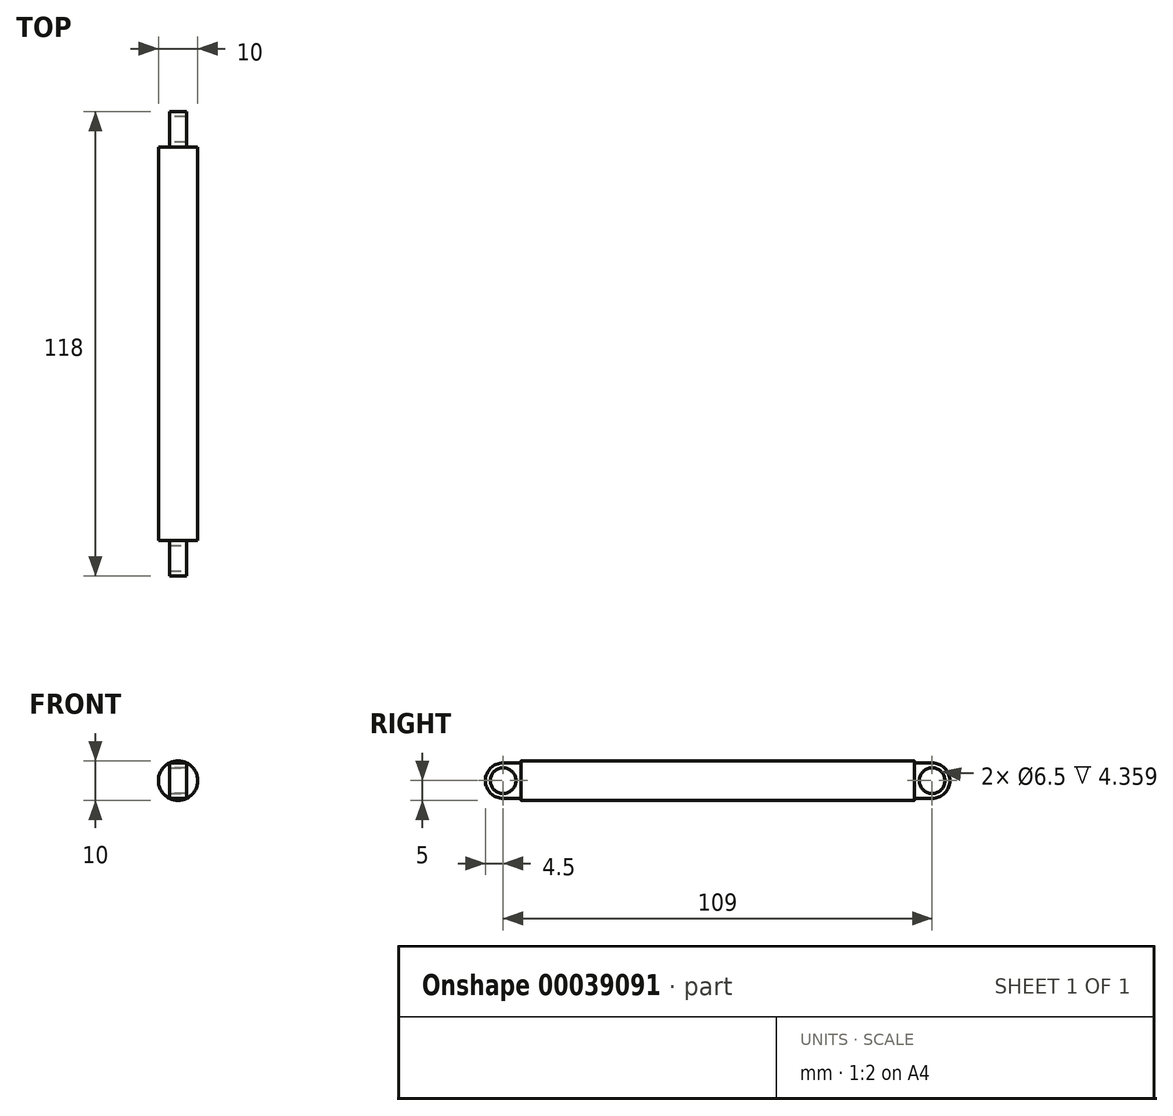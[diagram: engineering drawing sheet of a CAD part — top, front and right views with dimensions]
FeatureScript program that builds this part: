
annotation { "Feature Type Name" : "Feature", "Feature Type Description" : "" }
export const myFeature = defineFeature(function(context is Context, id is Id, definition is map)
    precondition{}
    {
        {
            var Q0;
            Q0=qCreatedBy(makeId("Top.planeOp"),FACE);
            var sketch = newSketch(context, id + "F0", { "sketchPlane" : qUnion([Q0])});
            skLineSegment(sketch, "E0.bottom", {"start": v(0, 100) * mm, "end": v(-5, 100) * mm});
            skLineSegment(sketch, "E0.top", {"start": v(0, 0) * mm, "end": v(-5, 0) * mm});
            skLineSegment(sketch, "E0.left", {"start": v(0, 100) * mm, "end": v(0, 0) * mm});
            skLineSegment(sketch, "E0.right", {"start": v(-5, 100) * mm, "end": v(-5, 0) * mm});
            skSolve(sketch);
        }
        {
            var Q0;
            Q0 = qSketchRegion(id + "F0", true);
            var Q1;
            Q1=sQuery(id+"F0.wireOp",EDGE,"E0.left");
            revolve(context, id + "F1", {"entities" : qUnion([Q0]), "axis" : qUnion([Q1]), "revolveType" : RevolveType.FULL});
        }
        {
            var Q0;
            Q0=makeQuery(id+"F1.opRevolve","SWEPT_FACE",FACE,{"disambiguationData":[OSD([sQuery(id+"F0.wireOp",EDGE,"E0.top")])]});
            var sketch = newSketch(context, id + "F2", { "sketchPlane" : qUnion([Q0])});
            skLineSegment(sketch, "E1.bottom", {"start": v(-2.18, 4.5) * mm, "end": v(2.18, 4.5) * mm});
            skLineSegment(sketch, "E1.top", {"start": v(-2.18, -4.5) * mm, "end": v(2.18, -4.5) * mm});
            skLineSegment(sketch, "E1.left", {"start": v(-2.18, 4.5) * mm, "end": v(-2.18, -4.5) * mm});
            skLineSegment(sketch, "E1.right", {"start": v(2.18, 4.5) * mm, "end": v(2.18, -4.5) * mm});
            skSolve(sketch);
        }
        {
            var Q0;
            Q0 = qSketchRegion(id + "F2", true);
            extrude(context, id + "F3", {"entities" : qUnion([Q0]), "operationType" : NewBodyOperationType.ADD, "depth" : 9 * mm});
        }
        {
            var Q0;
            Q0=makeQuery(id+"F3.opExtrude","SWEPT_FACE",FACE,{"disambiguationData":[OSD([sQuery(id+"F2.wireOp",EDGE,"E1.right")])]});
            var sketch = newSketch(context, id + "F4", { "sketchPlane" : qUnion([Q0])});
            skCircle(sketch, "E2", {"center": v(-4.5, 0) * mm, "radius": 3.25 * mm});
            skSolve(sketch);
        }
        {
            var Q0;
            Q0 = qSketchRegion(id + "F4", true);
            extrude(context, id + "F5", {"entities" : qUnion([Q0]), "operationType" : NewBodyOperationType.REMOVE, "oppositeDirection" : true, "depth" : 5 * mm});
        }
        {
            var Q0;
            Q0=makeQuery(id+"F3.opExtrude","CAP_EDGE",EDGE,{"disambiguationData":[OSD([sQuery(id+"F2.wireOp",EDGE,"E1.bottom")])],"isStart":false});
            var Q1;
            Q1=makeQuery(id+"F3.opExtrude","CAP_EDGE",EDGE,{"disambiguationData":[OSD([sQuery(id+"F2.wireOp",EDGE,"E1.top")])],"isStart":false});
            fillet(context, id + "F6", {"entities" : qUnion([Q0, Q1]), "radius" : 4.5 * mm, "tangentPropagation" : true, "allowEdgeOverflow" : false});
        }
        {
            var Q0;
            Q0=makeQuery(id+"F1.opRevolve","SWEPT_FACE",FACE,{"disambiguationData":[OSD([sQuery(id+"F0.wireOp",EDGE,"E0.bottom")])]});
            var sketch = newSketch(context, id + "F7", { "sketchPlane" : qUnion([Q0])});
            skLineSegment(sketch, "E3.bottom", {"start": v(-2.18, 4.5) * mm, "end": v(2.18, 4.5) * mm});
            skLineSegment(sketch, "E3.top", {"start": v(-2.18, -4.5) * mm, "end": v(2.18, -4.5) * mm});
            skLineSegment(sketch, "E3.left", {"start": v(-2.18, 4.5) * mm, "end": v(-2.18, -4.5) * mm});
            skLineSegment(sketch, "E3.right", {"start": v(2.18, 4.5) * mm, "end": v(2.18, -4.5) * mm});
            skSolve(sketch);
        }
        {
            var Q0;
            Q0 = qSketchRegion(id + "F7", true);
            extrude(context, id + "F8", {"entities" : qUnion([Q0]), "operationType" : NewBodyOperationType.ADD, "depth" : 9 * mm});
        }
        {
            var Q0;
            Q0=makeQuery(id+"F8.opExtrude","SWEPT_FACE",FACE,{"disambiguationData":[OSD([sQuery(id+"F7.wireOp",EDGE,"E3.right")])]});
            var sketch = newSketch(context, id + "F9", { "sketchPlane" : qUnion([Q0])});
            skCircle(sketch, "E4", {"center": v(-104.5, 0) * mm, "radius": 3.25 * mm});
            skSolve(sketch);
        }
        {
            var Q0;
            Q0 = qSketchRegion(id + "F9", true);
            extrude(context, id + "F10", {"entities" : qUnion([Q0]), "operationType" : NewBodyOperationType.REMOVE, "oppositeDirection" : true, "depth" : 5 * mm});
        }
        {
            var Q0;
            Q0=makeQuery(id+"F8.opExtrude","CAP_EDGE",EDGE,{"disambiguationData":[OSD([sQuery(id+"F7.wireOp",EDGE,"E3.bottom")])],"isStart":false});
            var Q1;
            Q1=makeQuery(id+"F8.opExtrude","CAP_EDGE",EDGE,{"disambiguationData":[OSD([sQuery(id+"F7.wireOp",EDGE,"E3.top")])],"isStart":false});
            fillet(context, id + "F11", {"entities" : qUnion([Q0, Q1]), "radius" : 4.5 * mm, "tangentPropagation" : true, "allowEdgeOverflow" : false});
        }
    });
